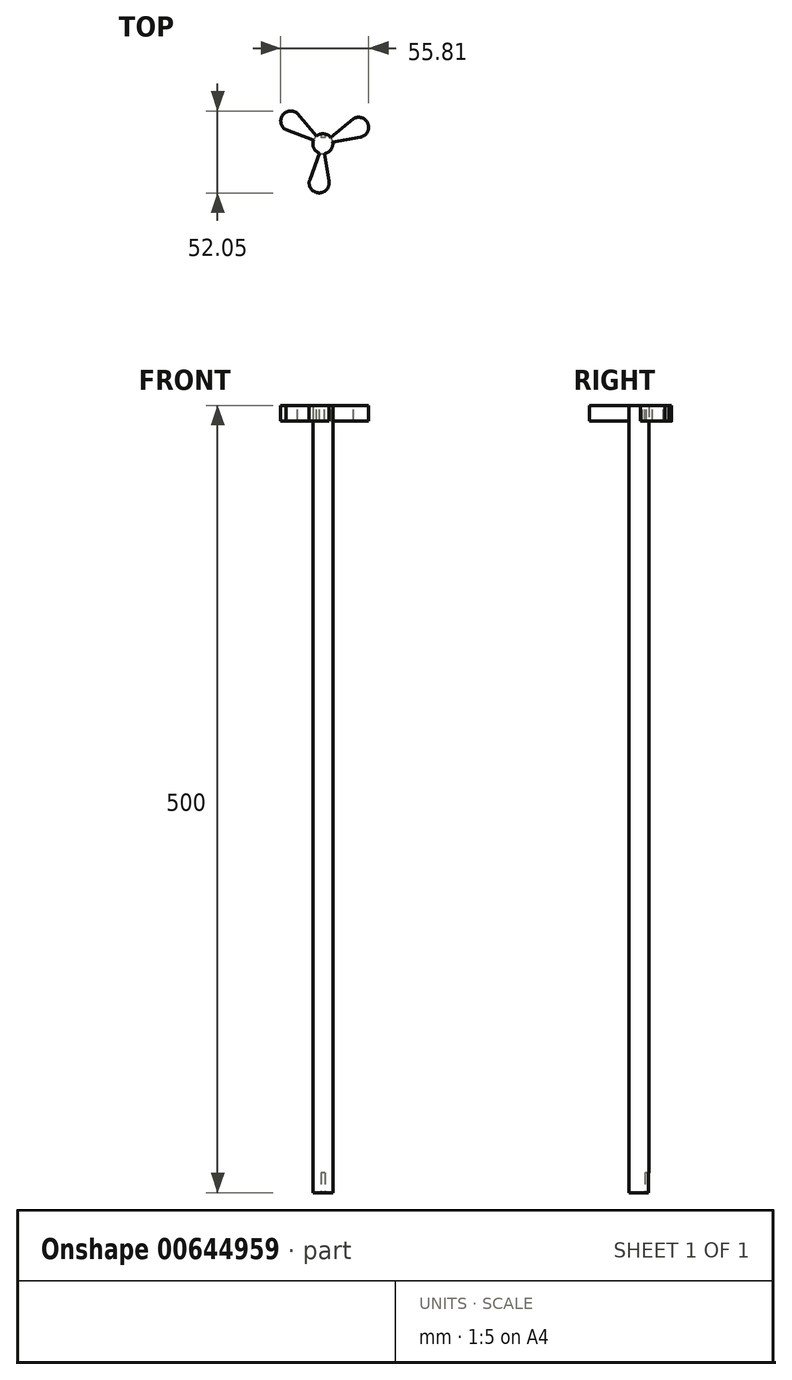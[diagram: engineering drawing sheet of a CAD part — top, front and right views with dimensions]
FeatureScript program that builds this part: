
annotation { "Feature Type Name" : "Feature", "Feature Type Description" : "" }
export const myFeature = defineFeature(function(context is Context, id is Id, definition is map)
    precondition{}
    {
        {
            var Q0;
            Q0=qCreatedBy(makeId("Top.planeOp"),FACE);
            var sketch = newSketch(context, id + "F0", { "sketchPlane" : qUnion([Q0])});
            skCircle(sketch, "E0", {"center": v(0, 0) * mm, "radius": 6.35 * mm});
            skSolve(sketch);
        }
        {
            var Q0;
            Q0 = qSketchRegion(id + "F0", true);
            extrude(context, id + "F1", {"entities" : qUnion([Q0]), "depth" : 500 * mm, "offsetDistance" : 25.4 * mm});
        }
        {
            var Q0;
            Q0=makeQuery(id+"F1.opExtrude","CAP_FACE",FACE,{"disambiguationData":[OSD([sQuery(id+"F0.wireOp",EDGE,"E0")])],"isStart":false});
            var sketch = newSketch(context, id + "F2", { "sketchPlane" : qUnion([Q0])});
            skArc(sketch, "E1", {"start": v(-15.05, 17.9) * mm, "mid": v(-25.57, 18.13) * mm, "end": v(-21.87, 8.28) * mm});
            skArc(sketch, "E2.1.0", {"start": v(-8.3, -22.71) * mm, "mid": v(-2.92, -31.21) * mm, "end": v(3.94, -23.86) * mm});
            skArc(sketch, "E2.2.0", {"start": v(23.82, 4.18) * mm, "mid": v(28.31, 13.44) * mm, "end": v(18.1, 14.8) * mm});
            skPoint(sketch, "E2.center", {"position": v(0, 0) * mm});
            skLineSegment(sketch, "E3", {"start": v(-16.1, 19.13) * mm, "end": v(0, 0) * mm});
            skLineSegment(sketch, "E4", {"start": v(19.36, 15.82) * mm, "end": v(0, 0) * mm});
            skLineSegment(sketch, "E5", {"start": v(0, 0) * mm, "end": v(24.62, 4.32) * mm});
            skLineSegment(sketch, "E6", {"start": v(-23.38, 8.86) * mm, "end": v(0, 0) * mm});
            skLineSegment(sketch, "E7", {"start": v(0, 0) * mm, "end": v(4.07, -24.67) * mm});
            skLineSegment(sketch, "E8", {"start": v(0, 0) * mm, "end": v(-8.57, -23.48) * mm});
            skSolve(sketch);
        }
        {
            var Q0;
            {var subQ1=sQuery(id+"F2.wireOp",EDGE,"E1");var subQ4=sQuery(id+"F2.wireOp",EDGE,"E3");var subQ8=makeQuery(id+"F2.imprint","INTERSECT",VERTEX,{"disambiguationData":[OD(1.0)],"derivedFrom":[subQ1,subQ4]});Q0=makeQuery(id+"F2.imprint","IMPRINT",FACE,{"disambiguationData":[TD([[makeQuery(id+"F2.imprint","IMPRINT",EDGE,{"disambiguationData":[TD([[subQ8,-1.0]])],"derivedFrom":subQ1}),1.0]])]});}
            var Q1;
            {var subQ0=sQuery(id+"F2.wireOp",EDGE,"E5");var subQ1=sQuery(id+"F2.wireOp",EDGE,"E2.2.0");var subQ2=makeQuery(id+"F2.imprint","INTERSECT",VERTEX,{"derivedFrom":[subQ1,subQ0]});Q1=makeQuery(id+"F2.imprint","IMPRINT",FACE,{"disambiguationData":[TD([[makeQuery(id+"F2.imprint","IMPRINT",EDGE,{"disambiguationData":[TD([[subQ2,-1.0]])],"derivedFrom":subQ1}),1.0]])]});}
            var Q2;
            {var subQ0=sQuery(id+"F2.wireOp",EDGE,"E2.1.0");Q2=makeQuery(id+"F2.imprint","IMPRINT",FACE,{"disambiguationData":[TD([[makeQuery(id+"F2.imprint","IMPRINT",EDGE,{"derivedFrom":subQ0}),1.0]])]});}
            extrude(context, id + "F3", {"entities" : qUnion([Q0, Q1, Q2]), "operationType" : NewBodyOperationType.ADD, "oppositeDirection" : true, "depth" : 10 * mm, "offsetDistance" : 25.4 * mm});
        }
        {
            var Q0;
            Q0=makeQuery(id+"F1.opExtrude","CAP_FACE",FACE,{"disambiguationData":[OSD([sQuery(id+"F0.wireOp",EDGE,"E0")])],"isStart":true});
            var sketch = newSketch(context, id + "F4", { "sketchPlane" : qUnion([Q0])});
            skLineSegment(sketch, "E9", {"start": v(0, 0) * mm, "end": v(0, -6.35) * mm});
            skLineSegment(sketch, "E10", {"start": v(1.27, -6.22) * mm, "end": v(1.27, -3.81) * mm});
            skLineSegment(sketch, "E11", {"start": v(-1.27, -6.22) * mm, "end": v(-1.27, -3.81) * mm});
            skLineSegment(sketch, "E12", {"start": v(1.27, -3.81) * mm, "end": v(-1.27, -3.81) * mm});
            skArc(sketch, "E13", {"start": v(1.27, -6.22) * mm, "mid": v(0, -6.35) * mm, "end": v(-1.27, -6.22) * mm});
            skSolve(sketch);
        }
        {
            var Q0;
            Q0 = qSketchRegion(id + "F4", true);
            extrude(context, id + "F5", {"entities" : qUnion([Q0]), "operationType" : NewBodyOperationType.REMOVE, "oppositeDirection" : true, "depth" : 12.7 * mm, "offsetDistance" : 25.4 * mm});
        }
    });
